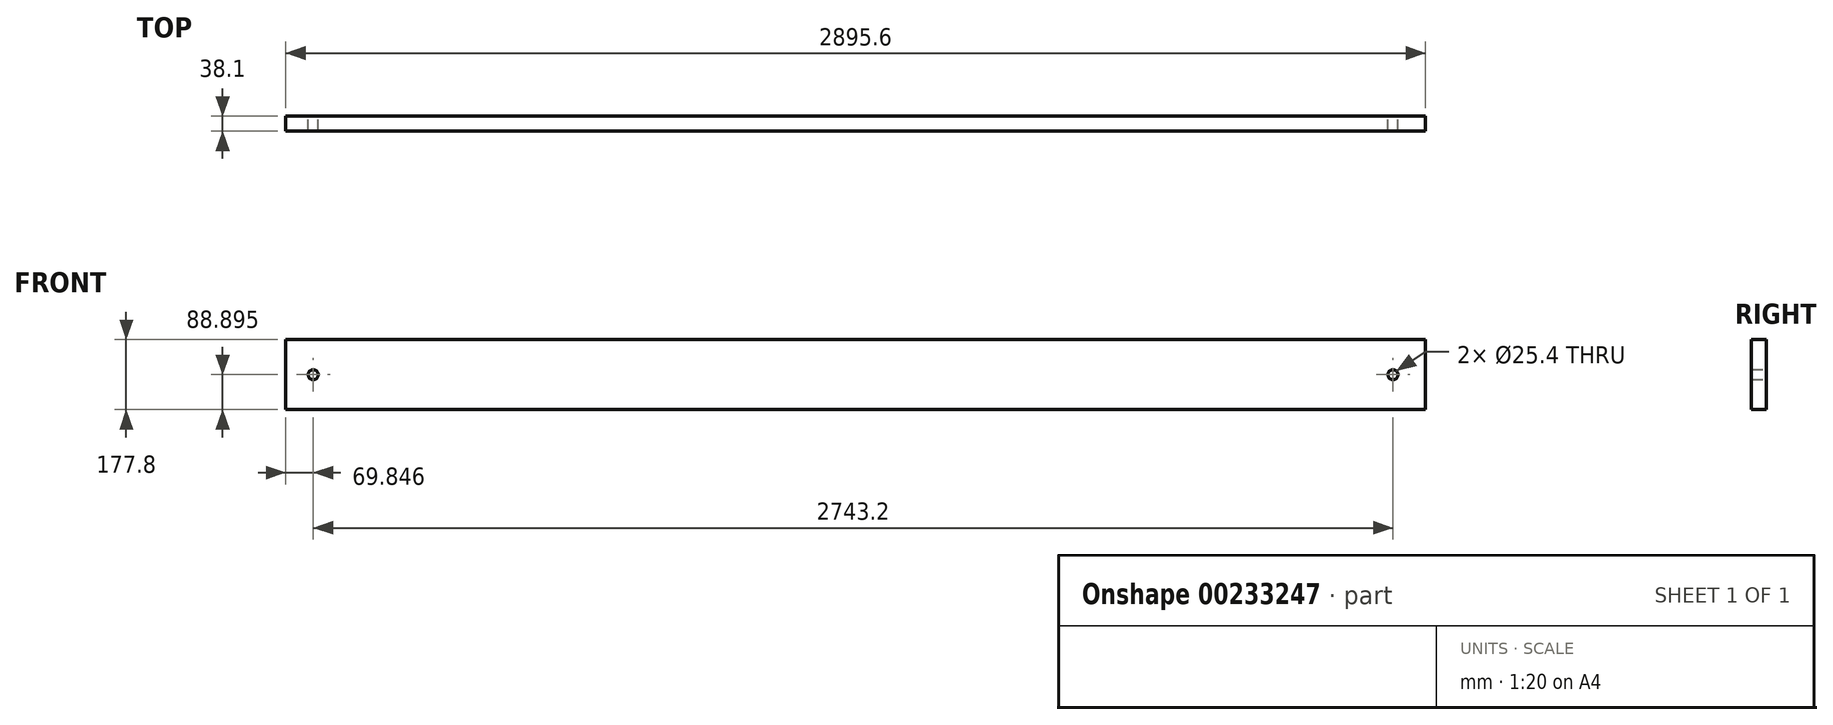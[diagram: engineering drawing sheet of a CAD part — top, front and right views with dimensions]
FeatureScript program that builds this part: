
annotation { "Feature Type Name" : "Feature", "Feature Type Description" : "" }
export const myFeature = defineFeature(function(context is Context, id is Id, definition is map)
    precondition{}
    {
        {
            var Q0;
            Q0=qCreatedBy(makeId("Front.planeOp"),FACE);
            var sketch = newSketch(context, id + "F0", { "sketchPlane" : qUnion([Q0])});
            skLineSegment(sketch, "E0.bottom", {"start": v(-1436, -392.5) * mm, "end": v(1459.6, -392.5) * mm});
            skLineSegment(sketch, "E0.top", {"start": v(-1436, -570.3) * mm, "end": v(1459.6, -570.3) * mm});
            skLineSegment(sketch, "E0.left", {"start": v(-1436, -392.5) * mm, "end": v(-1436, -570.3) * mm});
            skLineSegment(sketch, "E0.right", {"start": v(1459.6, -392.5) * mm, "end": v(1459.6, -570.3) * mm});
            skCircle(sketch, "E1", {"center": v(-1366.14, -481.4) * mm, "radius": 12.7 * mm});
            skCircle(sketch, "E2", {"center": v(1377.06, -481.4) * mm, "radius": 12.7 * mm});
            skSolve(sketch);
        }
        {
            var Q0;
            Q0 = qSketchRegion(id + "F0", true);
            extrude(context, id + "F1", {"entities" : qUnion([Q0]), "depth" : 38.1 * mm});
        }
    });
